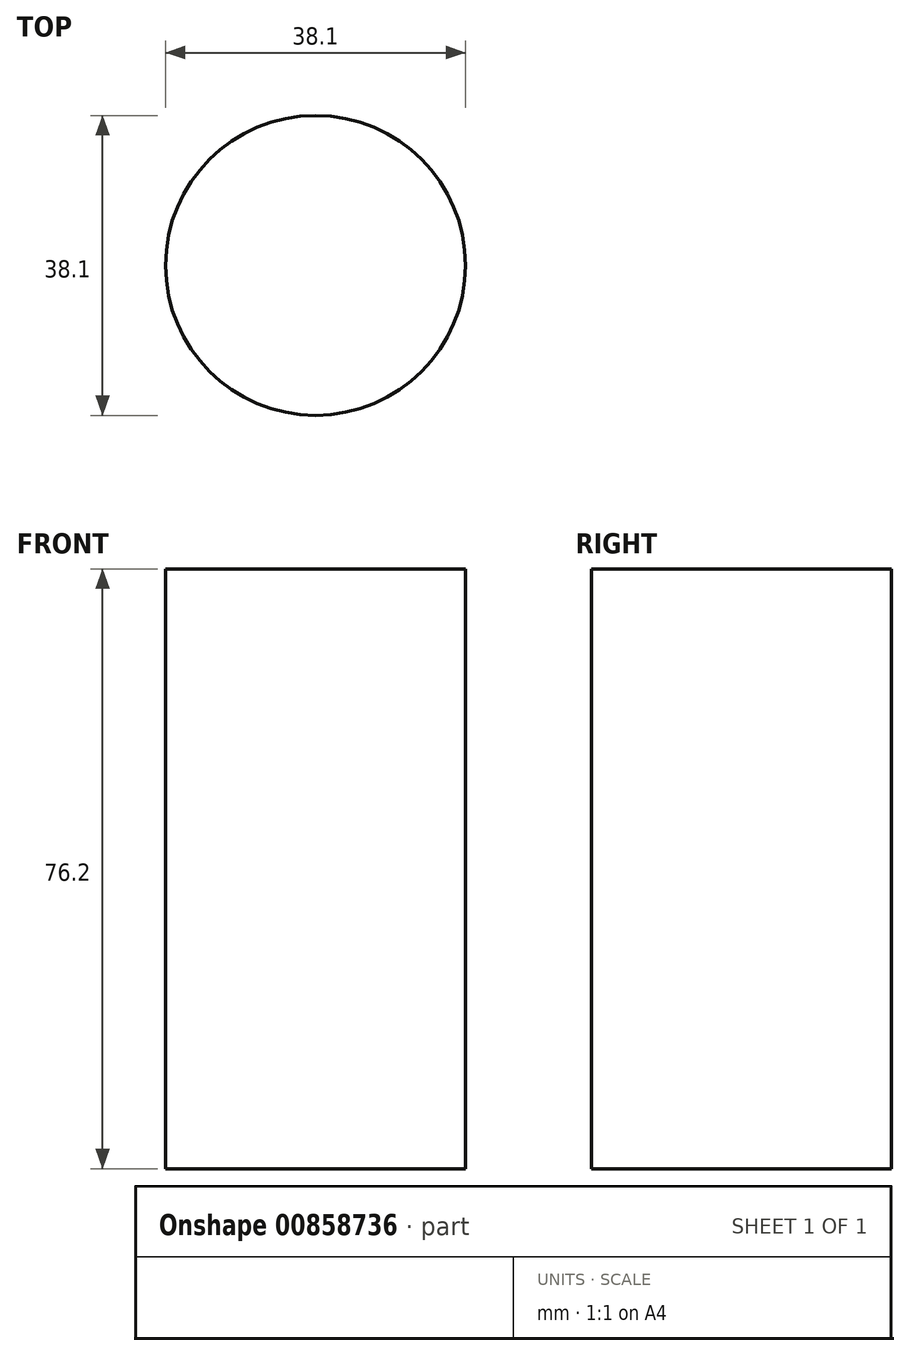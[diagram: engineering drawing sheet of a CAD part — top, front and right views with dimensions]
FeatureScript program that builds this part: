
annotation { "Feature Type Name" : "Feature", "Feature Type Description" : "" }
export const myFeature = defineFeature(function(context is Context, id is Id, definition is map)
    precondition{}
    {
        {
            var Q0;
            Q0=qCreatedBy(makeId("Top.planeOp"),FACE);
            var sketch = newSketch(context, id + "F0", { "sketchPlane" : qUnion([Q0])});
            skCircle(sketch, "E0", {"center": v(0, 0) * mm, "radius": 19.05 * mm});
            skSolve(sketch);
        }
        {
            var Q0;
            Q0 = qSketchRegion(id + "F0", true);
            extrude(context, id + "F1", {"entities" : qUnion([Q0]), "endBound" : BoundingType.SYMMETRIC, "depth" : 76.2 * mm, "offsetDistance" : 25.4 * mm});
        }
    });
